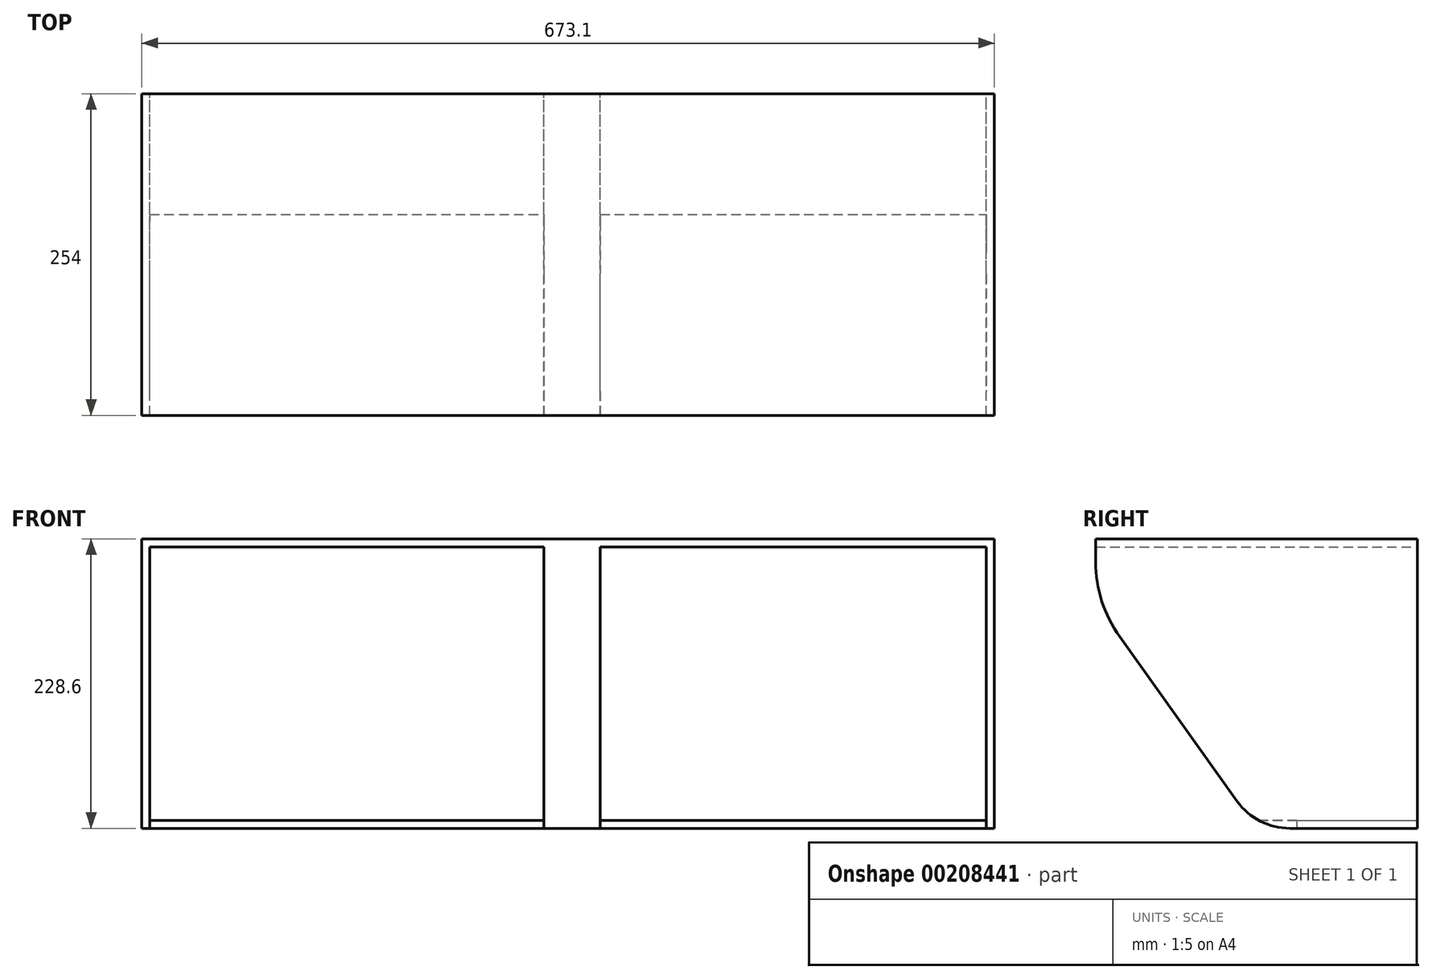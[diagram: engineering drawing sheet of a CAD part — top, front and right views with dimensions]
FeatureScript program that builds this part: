
annotation { "Feature Type Name" : "Feature", "Feature Type Description" : "" }
export const myFeature = defineFeature(function(context is Context, id is Id, definition is map)
    precondition{}
    {
        {
            var Q0;
            Q0=qCreatedBy(makeId("Front.planeOp"),FACE);
            var sketch = newSketch(context, id + "F0", { "sketchPlane" : qUnion([Q0])});
            skLineSegment(sketch, "E0.bottom", {"start": v(-330.2, 114.3) * mm, "end": v(330.2, 114.3) * mm});
            skLineSegment(sketch, "E0.top", {"start": v(-330.2, -114.3) * mm, "end": v(330.2, -114.3) * mm});
            skLineSegment(sketch, "E0.left", {"start": v(-330.2, 114.3) * mm, "end": v(-330.2, -114.3) * mm});
            skLineSegment(sketch, "E0.right", {"start": v(330.2, 114.3) * mm, "end": v(330.2, -114.3) * mm});
            skPoint(sketch, "E0.middle", {"position": v(0, 0) * mm});
            skLineSegment(sketch, "E1.0", {"start": v(-323.85, 107.95) * mm, "end": v(-323.85, -107.95) * mm});
            skLineSegment(sketch, "E1.1", {"start": v(-323.85, 107.95) * mm, "end": v(-3.18, 107.95) * mm});
            skLineSegment(sketch, "E1.2", {"start": v(323.85, 107.95) * mm, "end": v(323.85, -107.95) * mm});
            skLineSegment(sketch, "E1.3", {"start": v(-323.85, -107.95) * mm, "end": v(-3.18, -107.95) * mm});
            skLineSegment(sketch, "E2", {"start": v(-3.18, -107.95) * mm, "end": v(-3.18, 107.95) * mm});
            skLineSegment(sketch, "E3", {"start": v(3.17, -107.95) * mm, "end": v(3.17, 107.95) * mm});
            skPoint(sketch, "E4.orphan", {"position": v(0, 107.95) * mm});
            skLineSegment(sketch, "E5.trimOffspring", {"start": v(3.17, 107.95) * mm, "end": v(323.85, 107.95) * mm});
            skPoint(sketch, "E6.start.orphan", {"position": v(0, -107.95) * mm});
            skLineSegment(sketch, "E7.trimOffspring", {"start": v(3.17, -107.95) * mm, "end": v(323.85, -107.95) * mm});
            skSolve(sketch);
        }
        {
            var Q0;
            Q0=qSketchRegion(id+"F0",true);
            extrude(context, id + "F1", {"entities" : qUnion([Q0]), "depth" : 127 * mm});
        }
        {
            var Q0;
            Q0=makeQuery(id+"F1.opExtrude","SWEPT_FACE",FACE,{"disambiguationData":[OSD([sQuery(id+"F0.wireOp",EDGE,"E3")])]});
            extrude(context, id + "F2", {"entities" : qUnion([Q0]), "operationType" : NewBodyOperationType.ADD, "endBound" : BoundingType.SYMMETRIC, "depth" : 44.45 * mm});
        }
        {
            var Q0;
            Q0=makeQuery(id+"F1.opExtrude","SWEPT_FACE",FACE,{"disambiguationData":[OSD([sQuery(id+"F0.wireOp",EDGE,"E0.right")])]});
            extrude(context, id + "F3", {"entities" : qUnion([Q0]), "operationType" : NewBodyOperationType.ADD, "depth" : 6.35 * mm});
        }
        {
            var Q0;
            Q0=makeQuery(id+"F1.opExtrude","SWEPT_FACE",FACE,{"disambiguationData":[OSD([sQuery(id+"F0.wireOp",EDGE,"E1.2")])]});
            extrude(context, id + "F4", {"entities" : qUnion([Q0]), "operationType" : NewBodyOperationType.REMOVE, "oppositeDirection" : true, "depth" : 6.35 * mm});
        }
        {
            var Q0;
            Q0=makeQuery(id+"F1.opExtrude","SWEPT_FACE",FACE,{"disambiguationData":[OSD([sQuery(id+"F0.wireOp",EDGE,"E0.left")])]});
            extrude(context, id + "F5", {"entities" : qUnion([Q0]), "operationType" : NewBodyOperationType.ADD, "depth" : 6.35 * mm});
        }
        {
            var Q0;
            Q0=makeQuery(id+"F1.opExtrude","SWEPT_FACE",FACE,{"disambiguationData":[OSD([sQuery(id+"F0.wireOp",EDGE,"E1.0")])]});
            extrude(context, id + "F6", {"entities" : qUnion([Q0]), "operationType" : NewBodyOperationType.REMOVE, "oppositeDirection" : true, "depth" : 6.35 * mm});
        }
        {
            var Q0;
            {var subQ0=sQuery(id+"F0.wireOp",EDGE,"E0.left");var subQ1=sQuery(id+"F0.wireOp",EDGE,"E0.right");var subQ2=sQuery(id+"F0.wireOp",EDGE,"E3");Q0=makeQuery(id+"F5.boolean.opBoolean","MERGE",FACE,{"derivedFrom":[makeQuery(id+"F3.boolean.opBoolean","MERGE",FACE,{"derivedFrom":[makeQuery(id+"F2.boolean.opBoolean","MERGE",FACE,{"derivedFrom":[makeQuery(id+"F1.opExtrude","CAP_FACE",FACE,{"disambiguationData":[OSD([sQuery(id+"F0.wireOp",EDGE,"E0.bottom"),sQuery(id+"F0.wireOp",EDGE,"E0.top"),subQ0,subQ1,sQuery(id+"F0.wireOp",EDGE,"E1.0"),sQuery(id+"F0.wireOp",EDGE,"E1.1"),sQuery(id+"F0.wireOp",EDGE,"E1.2"),sQuery(id+"F0.wireOp",EDGE,"E1.3"),sQuery(id+"F0.wireOp",EDGE,"E2"),subQ2,sQuery(id+"F0.wireOp",EDGE,"E5.trimOffspring"),sQuery(id+"F0.wireOp",EDGE,"E7.trimOffspring")])],"isStart":false}),makeQuery(id+"F2.opExtrude","SWEPT_FACE",FACE,{"disambiguationData":[OSD([subQ2]),TDD([makeQuery(id+"F1.opExtrude","CAP_EDGE",EDGE,{"disambiguationData":[OSD([subQ2])],"isStart":false})])]})]}),makeQuery(id+"F3.opExtrude","SWEPT_FACE",FACE,{"disambiguationData":[OSD([subQ1]),TDD([makeQuery(id+"F1.opExtrude","CAP_EDGE",EDGE,{"disambiguationData":[OSD([subQ1])],"isStart":false})])]})]}),makeQuery(id+"F5.opExtrude","SWEPT_FACE",FACE,{"disambiguationData":[OSD([subQ0]),TDD([makeQuery(id+"F1.opExtrude","CAP_EDGE",EDGE,{"disambiguationData":[OSD([subQ0])],"isStart":false})])]})]});}
            var sketch = newSketch(context, id + "F7", { "sketchPlane" : qUnion([Q0])});
            skLineSegment(sketch, "E8.bottom", {"start": v(-330.2, -107.95) * mm, "end": v(-19.05, -107.95) * mm});
            skLineSegment(sketch, "E8.top", {"start": v(-330.2, -114.3) * mm, "end": v(-19.05, -114.3) * mm});
            skLineSegment(sketch, "E8.left", {"start": v(-330.2, -107.95) * mm, "end": v(-330.2, -114.3) * mm});
            skLineSegment(sketch, "E8.right", {"start": v(-19.05, -107.95) * mm, "end": v(-19.05, -114.3) * mm});
            skLineSegment(sketch, "E9.bottom", {"start": v(25.4, -107.95) * mm, "end": v(330.18, -107.95) * mm});
            skLineSegment(sketch, "E9.top", {"start": v(25.4, -114.3) * mm, "end": v(330.18, -114.3) * mm});
            skLineSegment(sketch, "E9.left", {"start": v(25.4, -107.95) * mm, "end": v(25.4, -114.3) * mm});
            skLineSegment(sketch, "E9.right", {"start": v(330.18, -107.95) * mm, "end": v(330.18, -114.3) * mm});
            skSolve(sketch);
        }
        {
            var Q0;
            Q0=qSketchRegion(id+"F7",true);
            extrude(context, id + "F8", {"entities" : qUnion([Q0]), "operationType" : NewBodyOperationType.REMOVE, "oppositeDirection" : true, "depth" : 31.75 * mm});
        }
        {
            var Q0;
            {var subQ0=sQuery(id+"F0.wireOp",EDGE,"E0.left");var subQ1=sQuery(id+"F0.wireOp",EDGE,"E0.right");var subQ2=sQuery(id+"F0.wireOp",EDGE,"E3");Q0=makeQuery(id+"F5.boolean.opBoolean","MERGE",FACE,{"derivedFrom":[makeQuery(id+"F3.boolean.opBoolean","MERGE",FACE,{"derivedFrom":[makeQuery(id+"F2.boolean.opBoolean","MERGE",FACE,{"derivedFrom":[makeQuery(id+"F1.opExtrude","CAP_FACE",FACE,{"disambiguationData":[OSD([sQuery(id+"F0.wireOp",EDGE,"E0.bottom"),sQuery(id+"F0.wireOp",EDGE,"E0.top"),subQ0,subQ1,sQuery(id+"F0.wireOp",EDGE,"E1.0"),sQuery(id+"F0.wireOp",EDGE,"E1.1"),sQuery(id+"F0.wireOp",EDGE,"E1.2"),sQuery(id+"F0.wireOp",EDGE,"E1.3"),sQuery(id+"F0.wireOp",EDGE,"E2"),subQ2,sQuery(id+"F0.wireOp",EDGE,"E5.trimOffspring"),sQuery(id+"F0.wireOp",EDGE,"E7.trimOffspring")])],"isStart":false}),makeQuery(id+"F2.opExtrude","SWEPT_FACE",FACE,{"disambiguationData":[OSD([subQ2]),TDD([makeQuery(id+"F1.opExtrude","CAP_EDGE",EDGE,{"disambiguationData":[OSD([subQ2])],"isStart":false})])]})]}),makeQuery(id+"F3.opExtrude","SWEPT_FACE",FACE,{"disambiguationData":[OSD([subQ1]),TDD([makeQuery(id+"F1.opExtrude","CAP_EDGE",EDGE,{"disambiguationData":[OSD([subQ1])],"isStart":false})])]})]}),makeQuery(id+"F5.opExtrude","SWEPT_FACE",FACE,{"disambiguationData":[OSD([subQ0]),TDD([makeQuery(id+"F1.opExtrude","CAP_EDGE",EDGE,{"disambiguationData":[OSD([subQ0])],"isStart":false})])]})]});}
            var sketch = newSketch(context, id + "F9", { "sketchPlane" : qUnion([Q0])});
            skLineSegment(sketch, "E10.0.0", {"start": v(-19.05, -114.3) * mm, "end": v(25.4, -114.3) * mm});
            skLineSegment(sketch, "E10.0.1", {"start": v(25.4, -114.3) * mm, "end": v(25.4, 107.95) * mm});
            skLineSegment(sketch, "E10.0.2", {"start": v(25.4, 107.95) * mm, "end": v(330.2, 107.95) * mm});
            skLineSegment(sketch, "E10.0.3", {"start": v(330.2, 107.95) * mm, "end": v(330.2, -107.95) * mm});
            skLineSegment(sketch, "E10.0.4", {"start": v(330.2, -107.95) * mm, "end": v(330.18, -107.95) * mm});
            skLineSegment(sketch, "E10.0.5", {"start": v(330.18, -107.95) * mm, "end": v(330.18, -114.3) * mm});
            skLineSegment(sketch, "E10.0.6", {"start": v(330.18, -114.3) * mm, "end": v(336.55, -114.3) * mm});
            skLineSegment(sketch, "E10.0.7", {"start": v(336.55, -114.3) * mm, "end": v(336.55, 114.3) * mm});
            skLineSegment(sketch, "E10.0.8", {"start": v(336.55, 114.3) * mm, "end": v(-336.55, 114.3) * mm});
            skLineSegment(sketch, "E10.0.9", {"start": v(-336.55, 114.3) * mm, "end": v(-336.55, -114.3) * mm});
            skLineSegment(sketch, "E10.0.10", {"start": v(-336.55, -114.3) * mm, "end": v(-330.2, -114.3) * mm});
            skLineSegment(sketch, "E10.0.11", {"start": v(-330.2, -114.3) * mm, "end": v(-330.2, 107.95) * mm});
            skLineSegment(sketch, "E10.0.12", {"start": v(-330.2, 107.95) * mm, "end": v(-19.05, 107.95) * mm});
            skLineSegment(sketch, "E10.0.13", {"start": v(-19.05, 107.95) * mm, "end": v(-19.05, -114.3) * mm});
            skSolve(sketch);
        }
        {
            var Q0;
            Q0=makeQuery(id+"F9.imprint","IMPRINT",FACE,{"disambiguationData":[TD([[makeQuery(id+"F9.imprint","IMPRINT",EDGE,{"derivedFrom":sQuery(id+"F9.wireOp",EDGE,"E10.0.0")}),1.0]])]});
            extrude(context, id + "F10", {"entities" : qUnion([Q0]), "operationType" : NewBodyOperationType.ADD, "depth" : 127 * mm});
        }
        {
            var Q0;
            Q0=makeQuery(id+"F10.opExtrude","CAP_EDGE",EDGE,{"disambiguationData":[OSD([sQuery(id+"F9.wireOp",EDGE,"E10.0.0")])],"isStart":false});
            var Q1;
            Q1=makeQuery(id+"F10.opExtrude","CAP_EDGE",EDGE,{"disambiguationData":[OSD([sQuery(id+"F9.wireOp",EDGE,"E10.0.10")])],"isStart":false});
            var Q2;
            Q2=makeQuery(id+"F10.opExtrude","CAP_EDGE",EDGE,{"disambiguationData":[OSD([sQuery(id+"F9.wireOp",EDGE,"E10.0.6")])],"isStart":false});
            chamfer(context, id + "F11", {"entities" : qUnion([Q0, Q1, Q2]), "chamferType" : ChamferType.TWO_OFFSETS, "width1" : 177.8 * mm, "oppositeDirection" : false, "width2" : 127 * mm, "tangentPropagation" : true});
        }
        {
            var Q0;
            {var subQ0=sQuery(id+"F9.wireOp",EDGE,"E10.0.0");Q0=makeQuery(id+"F11.opChamfer","BLEND_EDGE",EDGE,{"blendedFrom":[makeQuery(id+"F10.opExtrude","CAP_EDGE",EDGE,{"disambiguationData":[OSD([subQ0])],"isStart":false}),makeQuery(id+"F10.opExtrude","CAP_FACE",FACE,{"disambiguationData":[OSD([subQ0,sQuery(id+"F9.wireOp",EDGE,"E10.0.1"),sQuery(id+"F9.wireOp",EDGE,"E10.0.2"),sQuery(id+"F9.wireOp",EDGE,"E10.0.3"),sQuery(id+"F9.wireOp",EDGE,"E10.0.4"),sQuery(id+"F9.wireOp",EDGE,"E10.0.5"),sQuery(id+"F9.wireOp",EDGE,"E10.0.6"),sQuery(id+"F9.wireOp",EDGE,"E10.0.7"),sQuery(id+"F9.wireOp",EDGE,"E10.0.8"),sQuery(id+"F9.wireOp",EDGE,"E10.0.9"),sQuery(id+"F9.wireOp",EDGE,"E10.0.10"),sQuery(id+"F9.wireOp",EDGE,"E10.0.11"),sQuery(id+"F9.wireOp",EDGE,"E10.0.12"),sQuery(id+"F9.wireOp",EDGE,"E10.0.13")])],"isStart":false})],"blendedInto":[makeQuery(id+"F10.opExtrude","CAP_FACE",FACE,{"disambiguationData":[OSD([subQ0,sQuery(id+"F9.wireOp",EDGE,"E10.0.1"),sQuery(id+"F9.wireOp",EDGE,"E10.0.2"),sQuery(id+"F9.wireOp",EDGE,"E10.0.3"),sQuery(id+"F9.wireOp",EDGE,"E10.0.4"),sQuery(id+"F9.wireOp",EDGE,"E10.0.5"),sQuery(id+"F9.wireOp",EDGE,"E10.0.6"),sQuery(id+"F9.wireOp",EDGE,"E10.0.7"),sQuery(id+"F9.wireOp",EDGE,"E10.0.8"),sQuery(id+"F9.wireOp",EDGE,"E10.0.9"),sQuery(id+"F9.wireOp",EDGE,"E10.0.10"),sQuery(id+"F9.wireOp",EDGE,"E10.0.11"),sQuery(id+"F9.wireOp",EDGE,"E10.0.12"),sQuery(id+"F9.wireOp",EDGE,"E10.0.13")])],"isStart":false})]});}
            var Q1;
            {var subQ0=sQuery(id+"F9.wireOp",EDGE,"E10.0.10");Q1=makeQuery(id+"F11.opChamfer","BLEND_EDGE",EDGE,{"blendedFrom":[makeQuery(id+"F10.opExtrude","CAP_EDGE",EDGE,{"disambiguationData":[OSD([subQ0])],"isStart":false}),makeQuery(id+"F10.opExtrude","CAP_FACE",FACE,{"disambiguationData":[OSD([sQuery(id+"F9.wireOp",EDGE,"E10.0.0"),sQuery(id+"F9.wireOp",EDGE,"E10.0.1"),sQuery(id+"F9.wireOp",EDGE,"E10.0.2"),sQuery(id+"F9.wireOp",EDGE,"E10.0.3"),sQuery(id+"F9.wireOp",EDGE,"E10.0.4"),sQuery(id+"F9.wireOp",EDGE,"E10.0.5"),sQuery(id+"F9.wireOp",EDGE,"E10.0.6"),sQuery(id+"F9.wireOp",EDGE,"E10.0.7"),sQuery(id+"F9.wireOp",EDGE,"E10.0.8"),sQuery(id+"F9.wireOp",EDGE,"E10.0.9"),subQ0,sQuery(id+"F9.wireOp",EDGE,"E10.0.11"),sQuery(id+"F9.wireOp",EDGE,"E10.0.12"),sQuery(id+"F9.wireOp",EDGE,"E10.0.13")])],"isStart":false})],"blendedInto":[makeQuery(id+"F10.opExtrude","CAP_FACE",FACE,{"disambiguationData":[OSD([sQuery(id+"F9.wireOp",EDGE,"E10.0.0"),sQuery(id+"F9.wireOp",EDGE,"E10.0.1"),sQuery(id+"F9.wireOp",EDGE,"E10.0.2"),sQuery(id+"F9.wireOp",EDGE,"E10.0.3"),sQuery(id+"F9.wireOp",EDGE,"E10.0.4"),sQuery(id+"F9.wireOp",EDGE,"E10.0.5"),sQuery(id+"F9.wireOp",EDGE,"E10.0.6"),sQuery(id+"F9.wireOp",EDGE,"E10.0.7"),sQuery(id+"F9.wireOp",EDGE,"E10.0.8"),sQuery(id+"F9.wireOp",EDGE,"E10.0.9"),subQ0,sQuery(id+"F9.wireOp",EDGE,"E10.0.11"),sQuery(id+"F9.wireOp",EDGE,"E10.0.12"),sQuery(id+"F9.wireOp",EDGE,"E10.0.13")])],"isStart":false})]});}
            var Q2;
            {var subQ0=sQuery(id+"F9.wireOp",EDGE,"E10.0.6");Q2=makeQuery(id+"F11.opChamfer","BLEND_EDGE",EDGE,{"blendedFrom":[makeQuery(id+"F10.opExtrude","CAP_EDGE",EDGE,{"disambiguationData":[OSD([subQ0])],"isStart":false}),makeQuery(id+"F10.opExtrude","CAP_FACE",FACE,{"disambiguationData":[OSD([sQuery(id+"F9.wireOp",EDGE,"E10.0.0"),sQuery(id+"F9.wireOp",EDGE,"E10.0.1"),sQuery(id+"F9.wireOp",EDGE,"E10.0.2"),sQuery(id+"F9.wireOp",EDGE,"E10.0.3"),sQuery(id+"F9.wireOp",EDGE,"E10.0.4"),sQuery(id+"F9.wireOp",EDGE,"E10.0.5"),subQ0,sQuery(id+"F9.wireOp",EDGE,"E10.0.7"),sQuery(id+"F9.wireOp",EDGE,"E10.0.8"),sQuery(id+"F9.wireOp",EDGE,"E10.0.9"),sQuery(id+"F9.wireOp",EDGE,"E10.0.10"),sQuery(id+"F9.wireOp",EDGE,"E10.0.11"),sQuery(id+"F9.wireOp",EDGE,"E10.0.12"),sQuery(id+"F9.wireOp",EDGE,"E10.0.13")])],"isStart":false})],"blendedInto":[makeQuery(id+"F10.opExtrude","CAP_FACE",FACE,{"disambiguationData":[OSD([sQuery(id+"F9.wireOp",EDGE,"E10.0.0"),sQuery(id+"F9.wireOp",EDGE,"E10.0.1"),sQuery(id+"F9.wireOp",EDGE,"E10.0.2"),sQuery(id+"F9.wireOp",EDGE,"E10.0.3"),sQuery(id+"F9.wireOp",EDGE,"E10.0.4"),sQuery(id+"F9.wireOp",EDGE,"E10.0.5"),subQ0,sQuery(id+"F9.wireOp",EDGE,"E10.0.7"),sQuery(id+"F9.wireOp",EDGE,"E10.0.8"),sQuery(id+"F9.wireOp",EDGE,"E10.0.9"),sQuery(id+"F9.wireOp",EDGE,"E10.0.10"),sQuery(id+"F9.wireOp",EDGE,"E10.0.11"),sQuery(id+"F9.wireOp",EDGE,"E10.0.12"),sQuery(id+"F9.wireOp",EDGE,"E10.0.13")])],"isStart":false})]});}
            fillet(context, id + "F12", {"entities" : qUnion([Q0, Q1, Q2]), "radius" : 101.6 * mm, "tangentPropagation" : true, "allowEdgeOverflow" : false});
        }
        {
            var Q0;
            {var subQ0=sQuery(id+"F9.wireOp",EDGE,"E10.0.0");var subQ1=sQuery(id+"F0.wireOp",EDGE,"E0.top");Q0=makeQuery(id+"F11.opChamfer","BLEND_EDGE",EDGE,{"blendedFrom":[makeQuery(id+"F10.opExtrude","CAP_EDGE",EDGE,{"disambiguationData":[OSD([subQ0])],"isStart":false}),makeQuery(id+"F10.boolean.opBoolean","MERGE",FACE,{"derivedFrom":[makeQuery(id+"F5.boolean.opBoolean","MERGE",FACE,{"derivedFrom":[makeQuery(id+"F3.boolean.opBoolean","MERGE",FACE,{"derivedFrom":[makeQuery(id+"F1.opExtrude","SWEPT_FACE",FACE,{"disambiguationData":[OSD([subQ1])]}),makeQuery(id+"F3.opExtrude","SWEPT_FACE",FACE,{"disambiguationData":[OSD([subQ1,sQuery(id+"F0.wireOp",EDGE,"E0.right")])]})]}),makeQuery(id+"F5.opExtrude","SWEPT_FACE",FACE,{"disambiguationData":[OSD([subQ1,sQuery(id+"F0.wireOp",EDGE,"E0.left")])]})]}),makeQuery(id+"F10.opExtrude","SWEPT_FACE",FACE,{"disambiguationData":[OSD([subQ0])]}),makeQuery(id+"F10.opExtrude","SWEPT_FACE",FACE,{"disambiguationData":[OSD([sQuery(id+"F9.wireOp",EDGE,"E10.0.6")])]}),makeQuery(id+"F10.opExtrude","SWEPT_FACE",FACE,{"disambiguationData":[OSD([sQuery(id+"F9.wireOp",EDGE,"E10.0.10")])]})]})],"blendedInto":[makeQuery(id+"F10.boolean.opBoolean","MERGE",FACE,{"derivedFrom":[makeQuery(id+"F5.boolean.opBoolean","MERGE",FACE,{"derivedFrom":[makeQuery(id+"F3.boolean.opBoolean","MERGE",FACE,{"derivedFrom":[makeQuery(id+"F1.opExtrude","SWEPT_FACE",FACE,{"disambiguationData":[OSD([subQ1])]}),makeQuery(id+"F3.opExtrude","SWEPT_FACE",FACE,{"disambiguationData":[OSD([subQ1,sQuery(id+"F0.wireOp",EDGE,"E0.right")])]})]}),makeQuery(id+"F5.opExtrude","SWEPT_FACE",FACE,{"disambiguationData":[OSD([subQ1,sQuery(id+"F0.wireOp",EDGE,"E0.left")])]})]}),makeQuery(id+"F10.opExtrude","SWEPT_FACE",FACE,{"disambiguationData":[OSD([subQ0])]}),makeQuery(id+"F10.opExtrude","SWEPT_FACE",FACE,{"disambiguationData":[OSD([sQuery(id+"F9.wireOp",EDGE,"E10.0.6")])]}),makeQuery(id+"F10.opExtrude","SWEPT_FACE",FACE,{"disambiguationData":[OSD([sQuery(id+"F9.wireOp",EDGE,"E10.0.10")])]})]})]});}
            var Q1;
            {var subQ0=sQuery(id+"F9.wireOp",EDGE,"E10.0.10");var subQ1=sQuery(id+"F0.wireOp",EDGE,"E0.top");Q1=makeQuery(id+"F11.opChamfer","BLEND_EDGE",EDGE,{"blendedFrom":[makeQuery(id+"F10.opExtrude","CAP_EDGE",EDGE,{"disambiguationData":[OSD([subQ0])],"isStart":false}),makeQuery(id+"F10.boolean.opBoolean","MERGE",FACE,{"derivedFrom":[makeQuery(id+"F5.boolean.opBoolean","MERGE",FACE,{"derivedFrom":[makeQuery(id+"F3.boolean.opBoolean","MERGE",FACE,{"derivedFrom":[makeQuery(id+"F1.opExtrude","SWEPT_FACE",FACE,{"disambiguationData":[OSD([subQ1])]}),makeQuery(id+"F3.opExtrude","SWEPT_FACE",FACE,{"disambiguationData":[OSD([subQ1,sQuery(id+"F0.wireOp",EDGE,"E0.right")])]})]}),makeQuery(id+"F5.opExtrude","SWEPT_FACE",FACE,{"disambiguationData":[OSD([subQ1,sQuery(id+"F0.wireOp",EDGE,"E0.left")])]})]}),makeQuery(id+"F10.opExtrude","SWEPT_FACE",FACE,{"disambiguationData":[OSD([sQuery(id+"F9.wireOp",EDGE,"E10.0.0")])]}),makeQuery(id+"F10.opExtrude","SWEPT_FACE",FACE,{"disambiguationData":[OSD([sQuery(id+"F9.wireOp",EDGE,"E10.0.6")])]}),makeQuery(id+"F10.opExtrude","SWEPT_FACE",FACE,{"disambiguationData":[OSD([subQ0])]})]})],"blendedInto":[makeQuery(id+"F10.boolean.opBoolean","MERGE",FACE,{"derivedFrom":[makeQuery(id+"F5.boolean.opBoolean","MERGE",FACE,{"derivedFrom":[makeQuery(id+"F3.boolean.opBoolean","MERGE",FACE,{"derivedFrom":[makeQuery(id+"F1.opExtrude","SWEPT_FACE",FACE,{"disambiguationData":[OSD([subQ1])]}),makeQuery(id+"F3.opExtrude","SWEPT_FACE",FACE,{"disambiguationData":[OSD([subQ1,sQuery(id+"F0.wireOp",EDGE,"E0.right")])]})]}),makeQuery(id+"F5.opExtrude","SWEPT_FACE",FACE,{"disambiguationData":[OSD([subQ1,sQuery(id+"F0.wireOp",EDGE,"E0.left")])]})]}),makeQuery(id+"F10.opExtrude","SWEPT_FACE",FACE,{"disambiguationData":[OSD([sQuery(id+"F9.wireOp",EDGE,"E10.0.0")])]}),makeQuery(id+"F10.opExtrude","SWEPT_FACE",FACE,{"disambiguationData":[OSD([sQuery(id+"F9.wireOp",EDGE,"E10.0.6")])]}),makeQuery(id+"F10.opExtrude","SWEPT_FACE",FACE,{"disambiguationData":[OSD([subQ0])]})]})]});}
            var Q2;
            {var subQ0=sQuery(id+"F9.wireOp",EDGE,"E10.0.6");var subQ1=sQuery(id+"F0.wireOp",EDGE,"E0.top");Q2=makeQuery(id+"F11.opChamfer","BLEND_EDGE",EDGE,{"blendedFrom":[makeQuery(id+"F10.opExtrude","CAP_EDGE",EDGE,{"disambiguationData":[OSD([subQ0])],"isStart":false}),makeQuery(id+"F10.boolean.opBoolean","MERGE",FACE,{"derivedFrom":[makeQuery(id+"F5.boolean.opBoolean","MERGE",FACE,{"derivedFrom":[makeQuery(id+"F3.boolean.opBoolean","MERGE",FACE,{"derivedFrom":[makeQuery(id+"F1.opExtrude","SWEPT_FACE",FACE,{"disambiguationData":[OSD([subQ1])]}),makeQuery(id+"F3.opExtrude","SWEPT_FACE",FACE,{"disambiguationData":[OSD([subQ1,sQuery(id+"F0.wireOp",EDGE,"E0.right")])]})]}),makeQuery(id+"F5.opExtrude","SWEPT_FACE",FACE,{"disambiguationData":[OSD([subQ1,sQuery(id+"F0.wireOp",EDGE,"E0.left")])]})]}),makeQuery(id+"F10.opExtrude","SWEPT_FACE",FACE,{"disambiguationData":[OSD([sQuery(id+"F9.wireOp",EDGE,"E10.0.0")])]}),makeQuery(id+"F10.opExtrude","SWEPT_FACE",FACE,{"disambiguationData":[OSD([subQ0])]}),makeQuery(id+"F10.opExtrude","SWEPT_FACE",FACE,{"disambiguationData":[OSD([sQuery(id+"F9.wireOp",EDGE,"E10.0.10")])]})]})],"blendedInto":[makeQuery(id+"F10.boolean.opBoolean","MERGE",FACE,{"derivedFrom":[makeQuery(id+"F5.boolean.opBoolean","MERGE",FACE,{"derivedFrom":[makeQuery(id+"F3.boolean.opBoolean","MERGE",FACE,{"derivedFrom":[makeQuery(id+"F1.opExtrude","SWEPT_FACE",FACE,{"disambiguationData":[OSD([subQ1])]}),makeQuery(id+"F3.opExtrude","SWEPT_FACE",FACE,{"disambiguationData":[OSD([subQ1,sQuery(id+"F0.wireOp",EDGE,"E0.right")])]})]}),makeQuery(id+"F5.opExtrude","SWEPT_FACE",FACE,{"disambiguationData":[OSD([subQ1,sQuery(id+"F0.wireOp",EDGE,"E0.left")])]})]}),makeQuery(id+"F10.opExtrude","SWEPT_FACE",FACE,{"disambiguationData":[OSD([sQuery(id+"F9.wireOp",EDGE,"E10.0.0")])]}),makeQuery(id+"F10.opExtrude","SWEPT_FACE",FACE,{"disambiguationData":[OSD([subQ0])]}),makeQuery(id+"F10.opExtrude","SWEPT_FACE",FACE,{"disambiguationData":[OSD([sQuery(id+"F9.wireOp",EDGE,"E10.0.10")])]})]})]});}
            fillet(context, id + "F13", {"entities" : qUnion([Q0, Q1, Q2]), "radius" : 50.8 * mm, "tangentPropagation" : true, "allowEdgeOverflow" : false});
        }
    });
